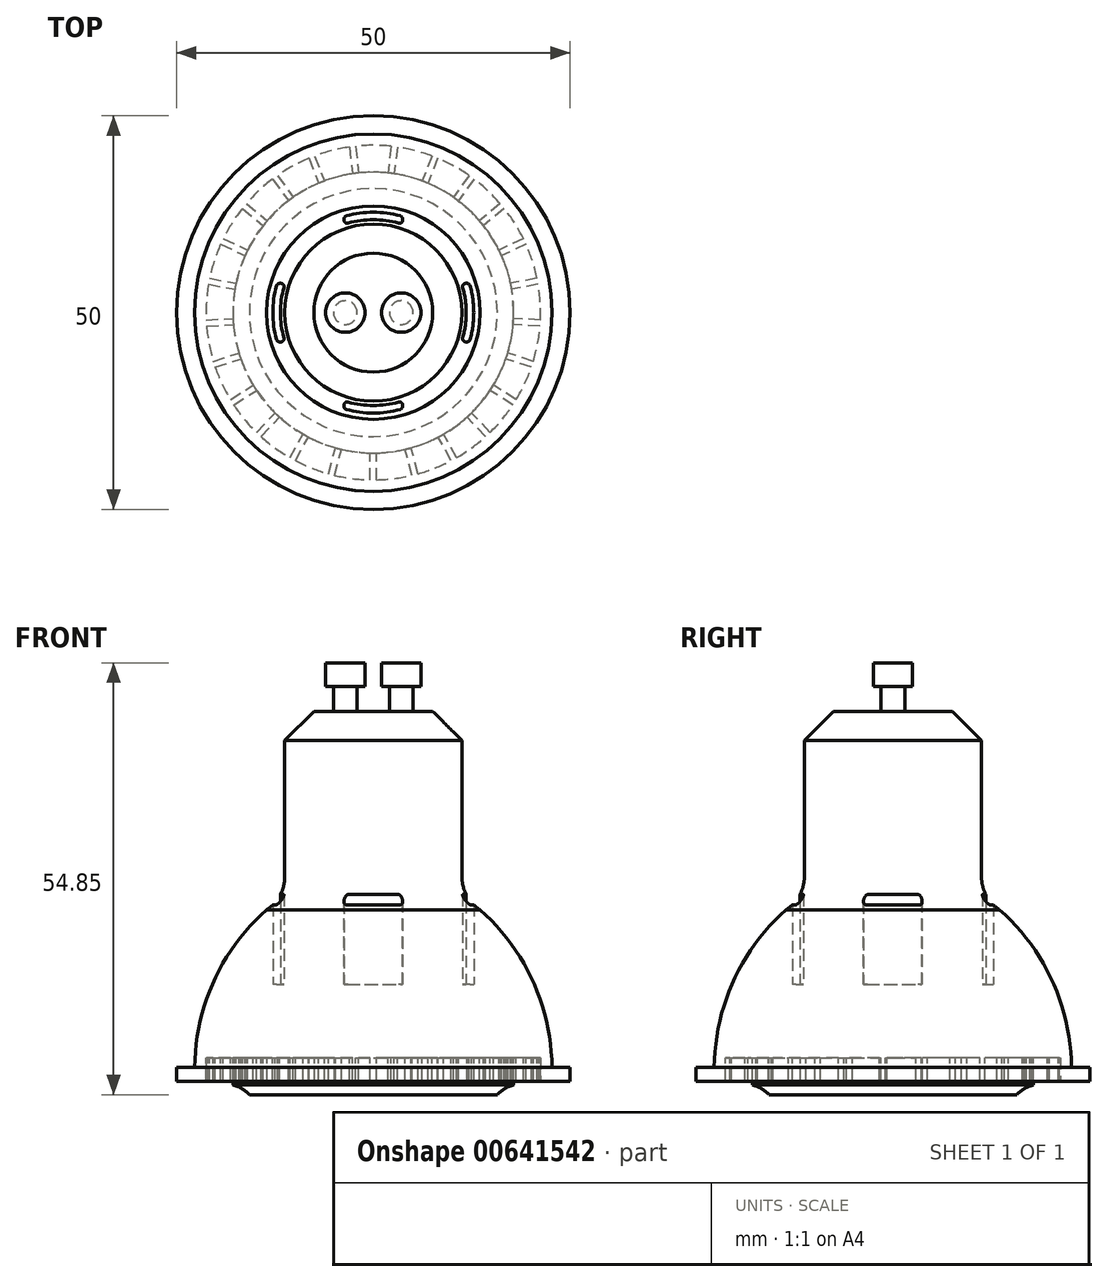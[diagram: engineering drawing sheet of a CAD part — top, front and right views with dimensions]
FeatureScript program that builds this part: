
annotation { "Feature Type Name" : "Feature", "Feature Type Description" : "" }
export const myFeature = defineFeature(function(context is Context, id is Id, definition is map)
    precondition{}
    {
        {
            var Q0;
            Q0=qCreatedBy(makeId("Front.planeOp"),FACE);
            var sketch = newSketch(context, id + "F0", { "sketchPlane" : qUnion([Q0])});
            skLineSegment(sketch, "E0", {"start": v(0, 34.68) * mm, "end": v(0, -12.32) * mm});
            skLineSegment(sketch, "E1", {"start": v(0, -12.32) * mm, "end": v(-25, -12.32) * mm});
            skLineSegment(sketch, "E2", {"start": v(-25, -12.32) * mm, "end": v(-25, -10.52) * mm});
            skLineSegment(sketch, "E3", {"start": v(-25, -10.52) * mm, "end": v(-22.7, -10.52) * mm});
            skLineSegment(sketch, "E4", {"start": v(0, 34.68) * mm, "end": v(-7.55, 34.68) * mm});
            skLineSegment(sketch, "E5", {"start": v(-7.55, 34.68) * mm, "end": v(-11.25, 30.98) * mm});
            skLineSegment(sketch, "E6", {"start": v(-11.25, 30.98) * mm, "end": v(-11.25, 13.7) * mm});
            skArc(sketch, "E7", {"start": v(-13.56, 9.48) * mm, "mid": v(-11.86, 11.3) * mm, "end": v(-11.25, 13.7) * mm});
            skArc(sketch, "E8", {"start": v(-13.56, 9.48) * mm, "mid": v(-20.24, 0.44) * mm, "end": v(-22.7, -10.52) * mm});
            skSolve(sketch);
        }
        {
            var Q0;
            Q0 = qSketchRegion(id + "F0", true);
            var Q1;
            Q1=sQuery(id+"F0.wireOp",EDGE,"E0");
            revolve(context, id + "F1", {"surfaceOperationType" : NewSurfaceOperationType.NEW, "entities" : qUnion([Q0]), "axis" : qUnion([Q1]), "revolveType" : RevolveType.FULL});
        }
        {
            var Q0;
            Q0=makeQuery(id+"F1.opRevolve","SWEPT_FACE",FACE,{"disambiguationData":[OSD([sQuery(id+"F0.wireOp",EDGE,"E4")])]});
            var sketch = newSketch(context, id + "F2", { "sketchPlane" : qUnion([Q0])});
            skCircle(sketch, "E9", {"center": v(-3.55, 0) * mm, "radius": 1.5 * mm});
            skLineSegment(sketch, "E10", {"start": v(0, 1.94) * mm, "end": v(0, -1.69) * mm});
            skCircle(sketch, "E11.MirrorC", {"center": v(3.55, 0) * mm, "radius": 1.5 * mm});
            skSolve(sketch);
        }
        {
            var Q0;
            Q0 = qSketchRegion(id + "F2", true);
            extrude(context, id + "F3", {"entities" : qUnion([Q0]), "operationType" : NewBodyOperationType.ADD, "depth" : 3.15 * mm, "offsetDistance" : 25 * mm});
        }
        {
            var Q0;
            Q0=makeQuery(id+"F3.opExtrude","CAP_FACE",FACE,{"disambiguationData":[OSD([sQuery(id+"F2.wireOp",EDGE,"E9")])],"isStart":false});
            var sketch = newSketch(context, id + "F4", { "sketchPlane" : qUnion([Q0])});
            skCircle(sketch, "E12", {"center": v(-3.55, 0) * mm, "radius": 2.5 * mm});
            skLineSegment(sketch, "E13", {"start": v(0, 3.4) * mm, "end": v(0, -2.9) * mm});
            skCircle(sketch, "E14.MirrorC", {"center": v(3.55, 0) * mm, "radius": 2.5 * mm});
            skSolve(sketch);
        }
        {
            var Q0;
            Q0 = qSketchRegion(id + "F4", true);
            extrude(context, id + "F5", {"entities" : qUnion([Q0]), "operationType" : NewBodyOperationType.ADD, "depth" : 3 * mm, "offsetDistance" : 25 * mm});
        }
        {
            var Q0;
            Q0=qCreatedBy(makeId("Front.planeOp"),FACE);
            var sketch = newSketch(context, id + "F6", { "sketchPlane" : qUnion([Q0])});
            skLineSegment(sketch, "E15", {"start": v(0, -12.32) * mm, "end": v(0, -14.02) * mm});
            skLineSegment(sketch, "E16", {"start": v(0, -14.02) * mm, "end": v(-15.75, -14.02) * mm});
            skArc(sketch, "E17", {"start": v(-15.75, -14.02) * mm, "mid": v(-16.7, -13.24) * mm, "end": v(-17.84, -12.8) * mm});
            skLineSegment(sketch, "E18", {"start": v(-17.84, -12.8) * mm, "end": v(-17.84, -12.32) * mm});
            skLineSegment(sketch, "E19", {"start": v(-17.84, -12.32) * mm, "end": v(0, -12.32) * mm});
            skSolve(sketch);
        }
        {
            var Q0;
            Q0 = qSketchRegion(id + "F6", true);
            var Q1;
            Q1=sQuery(id+"F6.wireOp",EDGE,"E15");
            revolve(context, id + "F7", {"operationType" : NewBodyOperationType.ADD, "entities" : qUnion([Q0]), "axis" : qUnion([Q1]), "revolveType" : RevolveType.FULL});
        }
        {
            var Q0;
            Q0=makeQuery(id+"F1.opRevolve","SWEPT_FACE",FACE,{"disambiguationData":[OSD([sQuery(id+"F0.wireOp",EDGE,"E1")])]});
            var sketch = newSketch(context, id + "F8", { "sketchPlane" : qUnion([Q0])});
            skCircle(sketch, "E20", {"center": v(0, 0) * mm, "radius": 17.84 * mm});
            skCircle(sketch, "E21", {"center": v(0, 0) * mm, "radius": 21.25 * mm});
            skSolve(sketch);
        }
        {
            var Q0;
            Q0 = qSketchRegion(id + "F8", true);
            extrude(context, id + "F9", {"entities" : qUnion([Q0]), "operationType" : NewBodyOperationType.REMOVE, "oppositeDirection" : true, "depth" : 3 * mm, "offsetDistance" : 25 * mm});
        }
        {
            var Q0;
            Q0=makeQuery(id+"F9.boolean.opBoolean","COPY",FACE,{"derivedFrom":makeQuery(id+"F9.opExtrude","CAP_FACE",FACE,{"disambiguationData":[OSD([sQuery(id+"F8.wireOp",EDGE,"E20"),sQuery(id+"F8.wireOp",EDGE,"E21")])],"isStart":false})});
            var sketch = newSketch(context, id + "F10", { "sketchPlane" : qUnion([Q0])});
            skLineSegment(sketch, "E22.left", {"start": v(-0.4, 21.25) * mm, "end": v(-0.4, 17.83) * mm});
            skLineSegment(sketch, "E22.right", {"start": v(0.4, 21.25) * mm, "end": v(0.4, 17.83) * mm});
            skArc(sketch, "E23", {"start": v(0.4, 17.83) * mm, "mid": v(0, 17.84) * mm, "end": v(-0.39, 17.83) * mm});
            skArc(sketch, "E24", {"start": v(0.39, 21.25) * mm, "mid": v(0, 21.25) * mm, "end": v(-0.39, 21.25) * mm});
            skArc(sketch, "E25.1.0", {"start": v(-4.9, 20.68) * mm, "mid": v(-5.28, 20.58) * mm, "end": v(-5.66, 20.48) * mm});
            skLineSegment(sketch, "E25.1.1", {"start": v(-4.9, 20.68) * mm, "end": v(-4.06, 17.37) * mm});
            skLineSegment(sketch, "E25.1.2", {"start": v(-5.66, 20.48) * mm, "end": v(-4.81, 17.17) * mm});
            skArc(sketch, "E25.1.3", {"start": v(-4.06, 17.37) * mm, "mid": v(-4.44, 17.28) * mm, "end": v(-4.81, 17.17) * mm});
            skArc(sketch, "E25.2.0", {"start": v(-9.9, 18.8) * mm, "mid": v(-10.24, 18.62) * mm, "end": v(-10.58, 18.43) * mm});
            skLineSegment(sketch, "E25.2.1", {"start": v(-9.9, 18.8) * mm, "end": v(-8.25, 15.81) * mm});
            skLineSegment(sketch, "E25.2.2", {"start": v(-10.58, 18.43) * mm, "end": v(-8.93, 15.44) * mm});
            skArc(sketch, "E25.2.3", {"start": v(-8.25, 15.81) * mm, "mid": v(-8.6, 15.63) * mm, "end": v(-8.93, 15.44) * mm});
            skArc(sketch, "E26.3.3.0", {"start": v(-14.26, 15.75) * mm, "mid": v(-14.55, 15.5) * mm, "end": v(-14.83, 15.22) * mm});
            skLineSegment(sketch, "E26.4.3.0", {"start": v(-14.26, 15.75) * mm, "end": v(-11.92, 13.27) * mm});
            skLineSegment(sketch, "E26.7.3.0", {"start": v(-14.83, 15.22) * mm, "end": v(-12.5, 12.73) * mm});
            skArc(sketch, "E26.10.3.0", {"start": v(-11.92, 13.27) * mm, "mid": v(-12.2, 13) * mm, "end": v(-12.5, 12.73) * mm});
            skArc(sketch, "E26.3.4.0", {"start": v(-17.73, 11.71) * mm, "mid": v(-17.94, 11.39) * mm, "end": v(-18.15, 11.06) * mm});
            skLineSegment(sketch, "E26.4.4.0", {"start": v(-17.73, 11.71) * mm, "end": v(-14.85, 9.88) * mm});
            skLineSegment(sketch, "E26.7.4.0", {"start": v(-18.15, 11.06) * mm, "end": v(-15.27, 9.23) * mm});
            skArc(sketch, "E26.10.4.0", {"start": v(-14.85, 9.88) * mm, "mid": v(-15.06, 9.56) * mm, "end": v(-15.27, 9.23) * mm});
            skArc(sketch, "E26.3.5.0", {"start": v(-20.09, 6.94) * mm, "mid": v(-20.2, 6.57) * mm, "end": v(-20.33, 6.2) * mm});
            skLineSegment(sketch, "E26.4.5.0", {"start": v(-20.09, 6.94) * mm, "end": v(-16.84, 5.88) * mm});
            skLineSegment(sketch, "E26.7.5.0", {"start": v(-20.33, 6.2) * mm, "end": v(-17.08, 5.14) * mm});
            skArc(sketch, "E26.10.5.0", {"start": v(-16.84, 5.88) * mm, "mid": v(-16.96, 5.51) * mm, "end": v(-17.08, 5.14) * mm});
            skArc(sketch, "E26.3.6.0", {"start": v(-21.18, 1.72) * mm, "mid": v(-21.2, 1.33) * mm, "end": v(-21.23, 0.94) * mm});
            skLineSegment(sketch, "E26.4.6.0", {"start": v(-21.18, 1.72) * mm, "end": v(-17.77, 1.5) * mm});
            skLineSegment(sketch, "E26.7.6.0", {"start": v(-21.23, 0.94) * mm, "end": v(-17.82, 0.73) * mm});
            skArc(sketch, "E26.10.6.0", {"start": v(-17.77, 1.5) * mm, "mid": v(-17.8, 1.12) * mm, "end": v(-17.82, 0.73) * mm});
            skArc(sketch, "E26.3.7.0", {"start": v(-20.94, -3.6) * mm, "mid": v(-20.87, -3.98) * mm, "end": v(-20.8, -4.36) * mm});
            skLineSegment(sketch, "E26.4.7.0", {"start": v(-20.94, -3.6) * mm, "end": v(-17.59, -2.96) * mm});
            skLineSegment(sketch, "E26.7.7.0", {"start": v(-20.8, -4.36) * mm, "end": v(-17.44, -3.72) * mm});
            skArc(sketch, "E26.10.7.0", {"start": v(-17.59, -2.96) * mm, "mid": v(-17.52, -3.34) * mm, "end": v(-17.44, -3.72) * mm});
            skArc(sketch, "E26.3.8.0", {"start": v(-19.4, -8.7) * mm, "mid": v(-19.23, -9.05) * mm, "end": v(-19.06, -9.4) * mm});
            skLineSegment(sketch, "E26.4.8.0", {"start": v(-19.4, -8.7) * mm, "end": v(-16.3, -7.24) * mm});
            skLineSegment(sketch, "E26.7.8.0", {"start": v(-19.06, -9.4) * mm, "end": v(-15.97, -7.95) * mm});
            skArc(sketch, "E26.10.8.0", {"start": v(-16.3, -7.24) * mm, "mid": v(-16.14, -7.6) * mm, "end": v(-15.97, -7.95) * mm});
            skArc(sketch, "E26.3.9.0", {"start": v(-16.62, -13.24) * mm, "mid": v(-16.37, -13.55) * mm, "end": v(-16.12, -13.84) * mm});
            skLineSegment(sketch, "E26.4.9.0", {"start": v(-16.62, -13.24) * mm, "end": v(-13.99, -11.07) * mm});
            skLineSegment(sketch, "E26.7.9.0", {"start": v(-16.12, -13.84) * mm, "end": v(-13.5, -11.67) * mm});
            skArc(sketch, "E26.10.9.0", {"start": v(-13.99, -11.07) * mm, "mid": v(-13.74, -11.37) * mm, "end": v(-13.5, -11.67) * mm});
            skArc(sketch, "E26.3.10.0", {"start": v(-12.8, -16.96) * mm, "mid": v(-12.5, -17.2) * mm, "end": v(-12.17, -17.42) * mm});
            skLineSegment(sketch, "E26.4.10.0", {"start": v(-12.8, -16.96) * mm, "end": v(-10.8, -14.2) * mm});
            skLineSegment(sketch, "E26.7.10.0", {"start": v(-12.17, -17.42) * mm, "end": v(-10.17, -14.66) * mm});
            skArc(sketch, "E26.10.10.0", {"start": v(-10.8, -14.2) * mm, "mid": v(-10.48, -14.43) * mm, "end": v(-10.17, -14.66) * mm});
            skArc(sketch, "E26.3.11.0", {"start": v(-8.18, -19.61) * mm, "mid": v(-7.82, -19.76) * mm, "end": v(-7.46, -19.9) * mm});
            skLineSegment(sketch, "E26.4.11.0", {"start": v(-8.18, -19.61) * mm, "end": v(-6.93, -16.44) * mm});
            skLineSegment(sketch, "E26.7.11.0", {"start": v(-7.46, -19.9) * mm, "end": v(-6.2, -16.72) * mm});
            skArc(sketch, "E26.10.11.0", {"start": v(-6.93, -16.44) * mm, "mid": v(-6.57, -16.58) * mm, "end": v(-6.2, -16.72) * mm});
            skArc(sketch, "E26.3.12.0", {"start": v(-3.05, -21.03) * mm, "mid": v(-2.66, -21.08) * mm, "end": v(-2.28, -21.13) * mm});
            skLineSegment(sketch, "E26.4.12.0", {"start": v(-3.05, -21.03) * mm, "end": v(-2.62, -17.64) * mm});
            skLineSegment(sketch, "E26.7.12.0", {"start": v(-2.28, -21.13) * mm, "end": v(-1.85, -17.74) * mm});
            skArc(sketch, "E26.10.12.0", {"start": v(-2.62, -17.64) * mm, "mid": v(-2.24, -17.7) * mm, "end": v(-1.85, -17.74) * mm});
            skArc(sketch, "E26.3.13.0", {"start": v(2.28, -21.13) * mm, "mid": v(2.66, -21.08) * mm, "end": v(3.05, -21.03) * mm});
            skLineSegment(sketch, "E26.4.13.0", {"start": v(2.28, -21.13) * mm, "end": v(1.85, -17.74) * mm});
            skLineSegment(sketch, "E26.7.13.0", {"start": v(3.05, -21.03) * mm, "end": v(2.62, -17.64) * mm});
            skArc(sketch, "E26.10.13.0", {"start": v(1.85, -17.74) * mm, "mid": v(2.24, -17.7) * mm, "end": v(2.62, -17.64) * mm});
            skArc(sketch, "E26.3.14.0", {"start": v(7.46, -19.9) * mm, "mid": v(7.82, -19.76) * mm, "end": v(8.18, -19.61) * mm});
            skLineSegment(sketch, "E26.4.14.0", {"start": v(7.46, -19.9) * mm, "end": v(6.2, -16.72) * mm});
            skLineSegment(sketch, "E26.7.14.0", {"start": v(8.18, -19.61) * mm, "end": v(6.93, -16.44) * mm});
            skArc(sketch, "E26.10.14.0", {"start": v(6.2, -16.72) * mm, "mid": v(6.57, -16.58) * mm, "end": v(6.93, -16.44) * mm});
            skArc(sketch, "E26.3.15.0", {"start": v(12.17, -17.42) * mm, "mid": v(12.5, -17.2) * mm, "end": v(12.8, -16.96) * mm});
            skLineSegment(sketch, "E26.4.15.0", {"start": v(12.17, -17.42) * mm, "end": v(10.17, -14.66) * mm});
            skLineSegment(sketch, "E26.7.15.0", {"start": v(12.8, -16.96) * mm, "end": v(10.8, -14.2) * mm});
            skArc(sketch, "E26.10.15.0", {"start": v(10.17, -14.66) * mm, "mid": v(10.48, -14.43) * mm, "end": v(10.8, -14.2) * mm});
            skArc(sketch, "E26.3.16.0", {"start": v(16.12, -13.84) * mm, "mid": v(16.37, -13.55) * mm, "end": v(16.62, -13.24) * mm});
            skLineSegment(sketch, "E26.4.16.0", {"start": v(16.12, -13.84) * mm, "end": v(13.5, -11.67) * mm});
            skLineSegment(sketch, "E26.7.16.0", {"start": v(16.62, -13.24) * mm, "end": v(13.99, -11.07) * mm});
            skArc(sketch, "E26.10.16.0", {"start": v(13.5, -11.67) * mm, "mid": v(13.74, -11.37) * mm, "end": v(13.99, -11.07) * mm});
            skArc(sketch, "E26.3.17.0", {"start": v(19.06, -9.4) * mm, "mid": v(19.23, -9.05) * mm, "end": v(19.4, -8.7) * mm});
            skLineSegment(sketch, "E26.4.17.0", {"start": v(19.06, -9.4) * mm, "end": v(15.97, -7.95) * mm});
            skLineSegment(sketch, "E26.7.17.0", {"start": v(19.4, -8.7) * mm, "end": v(16.3, -7.24) * mm});
            skArc(sketch, "E26.10.17.0", {"start": v(15.97, -7.95) * mm, "mid": v(16.14, -7.6) * mm, "end": v(16.3, -7.24) * mm});
            skArc(sketch, "E26.3.18.0", {"start": v(20.8, -4.36) * mm, "mid": v(20.87, -3.98) * mm, "end": v(20.94, -3.6) * mm});
            skLineSegment(sketch, "E26.4.18.0", {"start": v(20.8, -4.36) * mm, "end": v(17.44, -3.72) * mm});
            skLineSegment(sketch, "E26.7.18.0", {"start": v(20.94, -3.6) * mm, "end": v(17.59, -2.96) * mm});
            skArc(sketch, "E26.10.18.0", {"start": v(17.44, -3.72) * mm, "mid": v(17.52, -3.34) * mm, "end": v(17.59, -2.96) * mm});
            skArc(sketch, "E26.3.19.0", {"start": v(21.23, 0.94) * mm, "mid": v(21.2, 1.33) * mm, "end": v(21.18, 1.72) * mm});
            skLineSegment(sketch, "E26.4.19.0", {"start": v(21.23, 0.94) * mm, "end": v(17.82, 0.73) * mm});
            skLineSegment(sketch, "E26.7.19.0", {"start": v(21.18, 1.72) * mm, "end": v(17.77, 1.5) * mm});
            skArc(sketch, "E26.10.19.0", {"start": v(17.82, 0.73) * mm, "mid": v(17.8, 1.12) * mm, "end": v(17.77, 1.5) * mm});
            skArc(sketch, "E26.3.20.0", {"start": v(20.33, 6.2) * mm, "mid": v(20.2, 6.57) * mm, "end": v(20.09, 6.94) * mm});
            skLineSegment(sketch, "E26.4.20.0", {"start": v(20.33, 6.2) * mm, "end": v(17.08, 5.14) * mm});
            skLineSegment(sketch, "E26.7.20.0", {"start": v(20.09, 6.94) * mm, "end": v(16.84, 5.88) * mm});
            skArc(sketch, "E26.10.20.0", {"start": v(17.08, 5.14) * mm, "mid": v(16.96, 5.51) * mm, "end": v(16.84, 5.88) * mm});
            skArc(sketch, "E26.3.21.0", {"start": v(18.15, 11.06) * mm, "mid": v(17.94, 11.39) * mm, "end": v(17.73, 11.71) * mm});
            skLineSegment(sketch, "E26.4.21.0", {"start": v(18.15, 11.06) * mm, "end": v(15.27, 9.23) * mm});
            skLineSegment(sketch, "E26.7.21.0", {"start": v(17.73, 11.71) * mm, "end": v(14.85, 9.88) * mm});
            skArc(sketch, "E26.10.21.0", {"start": v(15.27, 9.23) * mm, "mid": v(15.06, 9.56) * mm, "end": v(14.85, 9.88) * mm});
            skArc(sketch, "E26.3.22.0", {"start": v(14.83, 15.22) * mm, "mid": v(14.55, 15.5) * mm, "end": v(14.26, 15.75) * mm});
            skLineSegment(sketch, "E26.4.22.0", {"start": v(14.83, 15.22) * mm, "end": v(12.5, 12.73) * mm});
            skLineSegment(sketch, "E26.7.22.0", {"start": v(14.26, 15.75) * mm, "end": v(11.92, 13.27) * mm});
            skArc(sketch, "E26.10.22.0", {"start": v(12.5, 12.73) * mm, "mid": v(12.2, 13) * mm, "end": v(11.92, 13.27) * mm});
            skArc(sketch, "E26.3.23.0", {"start": v(10.58, 18.43) * mm, "mid": v(10.24, 18.62) * mm, "end": v(9.9, 18.8) * mm});
            skLineSegment(sketch, "E26.4.23.0", {"start": v(10.58, 18.43) * mm, "end": v(8.93, 15.44) * mm});
            skLineSegment(sketch, "E26.7.23.0", {"start": v(9.9, 18.8) * mm, "end": v(8.25, 15.81) * mm});
            skArc(sketch, "E26.10.23.0", {"start": v(8.93, 15.44) * mm, "mid": v(8.6, 15.63) * mm, "end": v(8.25, 15.81) * mm});
            skArc(sketch, "E26.3.24.0", {"start": v(5.66, 20.48) * mm, "mid": v(5.28, 20.58) * mm, "end": v(4.9, 20.68) * mm});
            skLineSegment(sketch, "E26.4.24.0", {"start": v(5.66, 20.48) * mm, "end": v(4.81, 17.17) * mm});
            skLineSegment(sketch, "E26.7.24.0", {"start": v(4.9, 20.68) * mm, "end": v(4.06, 17.37) * mm});
            skArc(sketch, "E26.10.24.0", {"start": v(4.81, 17.17) * mm, "mid": v(4.44, 17.28) * mm, "end": v(4.06, 17.37) * mm});
            skSolve(sketch);
        }
        {
            var Q0;
            Q0 = qSketchRegion(id + "F10", true);
            var Q1;
            Q1=makeQuery(id+"F1.opRevolve","SWEPT_FACE",FACE,{"disambiguationData":[OSD([sQuery(id+"F0.wireOp",EDGE,"E1")])]});
            extrude(context, id + "F11", {"entities" : qUnion([Q0]), "operationType" : NewBodyOperationType.ADD, "endBound" : BoundingType.UP_TO_SURFACE, "depth" : 25 * mm, "endBoundEntityFace" : qUnion([Q1]), "offsetDistance" : 25 * mm});
        }
        {
            var Q0;
            Q0=qCreatedBy(makeId("Top.planeOp"),FACE);
            var sketch = newSketch(context, id + "F12", { "sketchPlane" : qUnion([Q0])});
            skArc(sketch, "E27", {"start": v(3.72, 11.2) * mm, "mid": v(0, 11.8) * mm, "end": v(-3.72, 11.2) * mm});
            skArc(sketch, "E28", {"start": v(3.72, 12.2) * mm, "mid": v(0, 12.76) * mm, "end": v(-3.72, 12.2) * mm});
            skLineSegment(sketch, "E29", {"start": v(-3.72, 12.2) * mm, "end": v(-3.72, 11.2) * mm});
            skLineSegment(sketch, "E30.MirrorCS", {"start": v(3.72, 12.2) * mm, "end": v(3.72, 11.2) * mm});
            skPoint(sketch, "E31.start.orphan", {"position": v(0, 15.57) * mm});
            skArc(sketch, "E32.1.0", {"start": v(-12.2, 3.72) * mm, "mid": v(-12.76, 0) * mm, "end": v(-12.2, -3.72) * mm});
            skLineSegment(sketch, "E32.1.1", {"start": v(-12.2, -3.72) * mm, "end": v(-11.2, -3.72) * mm});
            skArc(sketch, "E32.1.2", {"start": v(-11.2, 3.72) * mm, "mid": v(-11.8, 0) * mm, "end": v(-11.2, -3.72) * mm});
            skLineSegment(sketch, "E32.1.3", {"start": v(-12.2, 3.72) * mm, "end": v(-11.2, 3.72) * mm});
            skArc(sketch, "E32.2.0", {"start": v(-3.72, -12.2) * mm, "mid": v(0, -12.76) * mm, "end": v(3.72, -12.2) * mm});
            skLineSegment(sketch, "E32.2.1", {"start": v(3.72, -12.2) * mm, "end": v(3.72, -11.2) * mm});
            skArc(sketch, "E32.2.2", {"start": v(-3.72, -11.2) * mm, "mid": v(0, -11.8) * mm, "end": v(3.72, -11.2) * mm});
            skLineSegment(sketch, "E32.2.3", {"start": v(-3.72, -12.2) * mm, "end": v(-3.72, -11.2) * mm});
            skArc(sketch, "E32.3.0", {"start": v(12.2, -3.72) * mm, "mid": v(12.76, 0) * mm, "end": v(12.2, 3.72) * mm});
            skLineSegment(sketch, "E32.3.1", {"start": v(12.2, 3.72) * mm, "end": v(11.2, 3.72) * mm});
            skArc(sketch, "E32.3.2", {"start": v(11.2, -3.72) * mm, "mid": v(11.8, 0) * mm, "end": v(11.2, 3.72) * mm});
            skLineSegment(sketch, "E32.3.3", {"start": v(12.2, -3.72) * mm, "end": v(11.2, -3.72) * mm});
            skSolve(sketch);
        }
        {
            var Q0;
            Q0 = qSketchRegion(id + "F12", true);
            extrude(context, id + "F13", {"entities" : qUnion([Q0]), "operationType" : NewBodyOperationType.REMOVE, "depth" : 22.5 * mm, "offsetDistance" : 25 * mm});
        }
        {
            var Q0;
            Q0=makeQuery(id+"F13.boolean.opBoolean","COPY",EDGE,{"derivedFrom":makeQuery(id+"F13.opExtrude","SWEPT_EDGE",EDGE,{"disambiguationData":[OSD([sQuery(id+"F12.wireOp",EDGE,"E27"),sQuery(id+"F12.wireOp",EDGE,"E29")])]})});
            var Q1;
            Q1=makeQuery(id+"F13.boolean.opBoolean","COPY",EDGE,{"derivedFrom":makeQuery(id+"F13.opExtrude","SWEPT_EDGE",EDGE,{"disambiguationData":[OSD([sQuery(id+"F12.wireOp",EDGE,"E28"),sQuery(id+"F12.wireOp",EDGE,"E29")])]})});
            var Q2;
            Q2=makeQuery(id+"F13.boolean.opBoolean","COPY",EDGE,{"derivedFrom":makeQuery(id+"F13.opExtrude","SWEPT_EDGE",EDGE,{"disambiguationData":[OSD([sQuery(id+"F12.wireOp",EDGE,"E27"),sQuery(id+"F12.wireOp",EDGE,"E30.MirrorCS")])]})});
            var Q3;
            Q3=makeQuery(id+"F13.boolean.opBoolean","COPY",EDGE,{"derivedFrom":makeQuery(id+"F13.opExtrude","SWEPT_EDGE",EDGE,{"disambiguationData":[OSD([sQuery(id+"F12.wireOp",EDGE,"E28"),sQuery(id+"F12.wireOp",EDGE,"E30.MirrorCS")])]})});
            var Q4;
            Q4=makeQuery(id+"F13.boolean.opBoolean","COPY",EDGE,{"derivedFrom":makeQuery(id+"F13.opExtrude","SWEPT_EDGE",EDGE,{"disambiguationData":[OSD([sQuery(id+"F12.wireOp",EDGE,"E32.1.0"),sQuery(id+"F12.wireOp",EDGE,"E32.1.3")])]})});
            var Q5;
            Q5=makeQuery(id+"F13.boolean.opBoolean","COPY",EDGE,{"derivedFrom":makeQuery(id+"F13.opExtrude","SWEPT_EDGE",EDGE,{"disambiguationData":[OSD([sQuery(id+"F12.wireOp",EDGE,"E32.1.2"),sQuery(id+"F12.wireOp",EDGE,"E32.1.3")])]})});
            var Q6;
            Q6=makeQuery(id+"F13.boolean.opBoolean","COPY",EDGE,{"derivedFrom":makeQuery(id+"F13.opExtrude","SWEPT_EDGE",EDGE,{"disambiguationData":[OSD([sQuery(id+"F12.wireOp",EDGE,"E32.1.1"),sQuery(id+"F12.wireOp",EDGE,"E32.1.2")])]})});
            var Q7;
            Q7=makeQuery(id+"F13.boolean.opBoolean","COPY",EDGE,{"derivedFrom":makeQuery(id+"F13.opExtrude","SWEPT_EDGE",EDGE,{"disambiguationData":[OSD([sQuery(id+"F12.wireOp",EDGE,"E32.1.0"),sQuery(id+"F12.wireOp",EDGE,"E32.1.1")])]})});
            var Q8;
            Q8=makeQuery(id+"F13.boolean.opBoolean","COPY",EDGE,{"derivedFrom":makeQuery(id+"F13.opExtrude","SWEPT_EDGE",EDGE,{"disambiguationData":[OSD([sQuery(id+"F12.wireOp",EDGE,"E32.3.1"),sQuery(id+"F12.wireOp",EDGE,"E32.3.2")])]})});
            var Q9;
            Q9=makeQuery(id+"F13.boolean.opBoolean","COPY",EDGE,{"derivedFrom":makeQuery(id+"F13.opExtrude","SWEPT_EDGE",EDGE,{"disambiguationData":[OSD([sQuery(id+"F12.wireOp",EDGE,"E32.3.2"),sQuery(id+"F12.wireOp",EDGE,"E32.3.3")])]})});
            var Q10;
            Q10=makeQuery(id+"F13.boolean.opBoolean","COPY",EDGE,{"derivedFrom":makeQuery(id+"F13.opExtrude","SWEPT_EDGE",EDGE,{"disambiguationData":[OSD([sQuery(id+"F12.wireOp",EDGE,"E32.3.0"),sQuery(id+"F12.wireOp",EDGE,"E32.3.3")])]})});
            var Q11;
            Q11=makeQuery(id+"F13.boolean.opBoolean","COPY",EDGE,{"derivedFrom":makeQuery(id+"F13.opExtrude","SWEPT_EDGE",EDGE,{"disambiguationData":[OSD([sQuery(id+"F12.wireOp",EDGE,"E32.3.0"),sQuery(id+"F12.wireOp",EDGE,"E32.3.1")])]})});
            var Q12;
            Q12=makeQuery(id+"F13.boolean.opBoolean","COPY",EDGE,{"derivedFrom":makeQuery(id+"F13.opExtrude","SWEPT_EDGE",EDGE,{"disambiguationData":[OSD([sQuery(id+"F12.wireOp",EDGE,"E32.2.0"),sQuery(id+"F12.wireOp",EDGE,"E32.2.3")])]})});
            var Q13;
            Q13=makeQuery(id+"F13.boolean.opBoolean","COPY",EDGE,{"derivedFrom":makeQuery(id+"F13.opExtrude","SWEPT_EDGE",EDGE,{"disambiguationData":[OSD([sQuery(id+"F12.wireOp",EDGE,"E32.2.2"),sQuery(id+"F12.wireOp",EDGE,"E32.2.3")])]})});
            var Q14;
            Q14=makeQuery(id+"F13.boolean.opBoolean","COPY",EDGE,{"derivedFrom":makeQuery(id+"F13.opExtrude","SWEPT_EDGE",EDGE,{"disambiguationData":[OSD([sQuery(id+"F12.wireOp",EDGE,"E32.2.1"),sQuery(id+"F12.wireOp",EDGE,"E32.2.2")])]})});
            var Q15;
            Q15=makeQuery(id+"F13.boolean.opBoolean","COPY",EDGE,{"derivedFrom":makeQuery(id+"F13.opExtrude","SWEPT_EDGE",EDGE,{"disambiguationData":[OSD([sQuery(id+"F12.wireOp",EDGE,"E32.2.0"),sQuery(id+"F12.wireOp",EDGE,"E32.2.1")])]})});
            fillet(context, id + "F14", {"entities" : qUnion([Q0, Q1, Q2, Q3, Q4, Q5, Q6, Q7, Q8, Q9, Q10, Q11, Q12, Q13, Q14, Q15]), "radius" : 0.4 * mm, "tangentPropagation" : true, "allowEdgeOverflow" : false});
        }
    });
